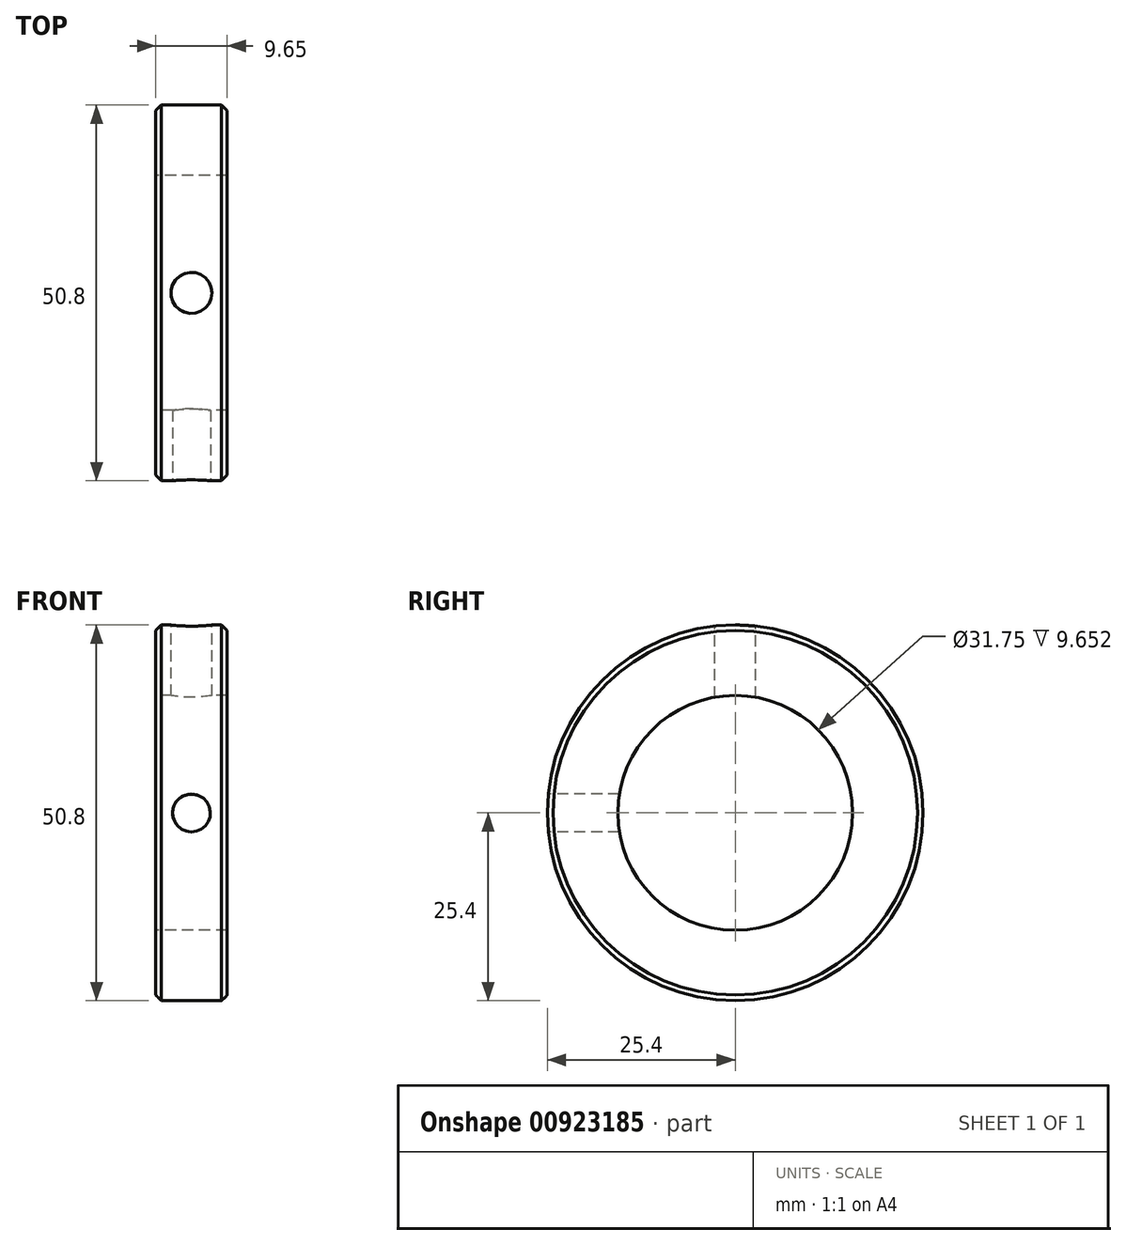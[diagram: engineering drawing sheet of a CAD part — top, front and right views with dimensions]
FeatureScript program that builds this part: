
annotation { "Feature Type Name" : "Feature", "Feature Type Description" : "" }
export const myFeature = defineFeature(function(context is Context, id is Id, definition is map)
    precondition{}
    {
        {
            var Q0;
            Q0=qCreatedBy(makeId("Right.planeOp"),FACE);
            var sketch = newSketch(context, id + "F0", { "sketchPlane" : qUnion([Q0])});
            skCircle(sketch, "E0", {"center": v(0, 0) * mm, "radius": 25.4 * mm});
            skCircle(sketch, "E1", {"center": v(0, 0) * mm, "radius": 15.88 * mm});
            skSolve(sketch);
        }
        {
            var Q0;
            Q0 = qSketchRegion(id + "F0", true);
            extrude(context, id + "F1", {"entities" : qUnion([Q0]), "depth" : 9.65 * mm, "offsetDistance" : 25.4 * mm});
        }
        {
            var Q0;
            Q0=makeQuery(id+"F1.opExtrude","CAP_EDGE",EDGE,{"disambiguationData":[OSD([sQuery(id+"F0.wireOp",EDGE,"E0")])],"isStart":false});
            chamfer(context, id + "F2", {"entities" : qUnion([Q0]), "width" : 0.76 * mm, "tangentPropagation" : true});
        }
        {
            var Q0;
            Q0=qCreatedBy(makeId("Front.planeOp"),FACE);
            cPlane(context, id + "F3", {"entities" : qUnion([Q0]), "cplaneType" : CPlaneType.OFFSET, "offset" : 25.4 * mm, "width" : 152.4 * mm, "height" : 152.4 * mm});
        }
        {
            var Q0;
            Q0=qCreatedBy(id+"F3.planeOp",FACE);
            var sketch = newSketch(context, id + "F4", { "sketchPlane" : qUnion([Q0])});
            skCircle(sketch, "E2", {"center": v(4.83, 0) * mm, "radius": 3.18 * mm});
            skSolve(sketch);
        }
        {
            var Q0;
            Q0=qCreatedBy(makeId("Top.planeOp"),FACE);
            cPlane(context, id + "F5", {"entities" : qUnion([Q0]), "cplaneType" : CPlaneType.OFFSET, "offset" : 25.4 * mm, "width" : 152.4 * mm, "height" : 152.4 * mm});
        }
        {
            var Q0;
            Q0=qCreatedBy(id+"F5.planeOp",FACE);
            var sketch = newSketch(context, id + "F6", { "sketchPlane" : qUnion([Q0])});
            skCircle(sketch, "E3", {"center": v(4.83, 0) * mm, "radius": 3.18 * mm});
            skSolve(sketch);
        }
        {
            var Q0;
            Q0=makeQuery(id+"F1.opExtrude","CAP_EDGE",EDGE,{"disambiguationData":[OSD([sQuery(id+"F0.wireOp",EDGE,"E0")])],"isStart":true});
            chamfer(context, id + "F7", {"entities" : qUnion([Q0]), "width" : 0.76 * mm, "tangentPropagation" : true});
        }
        {
            var Q0;
            Q0=sQuery(id+"F6.wireOp",VERTEX,"E3.center");
            var Q1;
            Q1=makeQuery(id+"F1.opExtrude","SWEPT_BODY",BODY,{"disambiguationData":[OSD([sQuery(id+"F0.wireOp",EDGE,"E0"),sQuery(id+"F0.wireOp",EDGE,"E1")])]});
            hole(context, id + "F8", {"style" : HoleStyle.SIMPLE, "endStyle" : HoleEndStyle.BLIND, "standardTappedOrClearance" : lookupTablePath({ "standard" : "ANSI", "engagement" : "50%", "pitch" : "20 tpi", "size" : "1/4", "type" : "Tapped" }), "standardBlindInLast" : lookupTablePath({ "standard" : "ANSI", "fit" : "Free", "engagement" : "50%", "pitch" : "20 tpi", "size" : "1/4", "type" : "Clearance & tapped" }), "holeDiameter" : 5.56 * mm, "majorDiameter" : 6.35 * mm, "showTappedDepth" : true, "holeDepth" : 16.51 * mm, "tappedDepth" : 10.16 * mm, "tapClearance" : 5, "startFromSketch" : true, "locations" : qUnion([Q0]), "scope" : qUnion([Q1])});
        }
        {
            var Q0;
            Q0=sQuery(id+"F4.wireOp",VERTEX,"E2.center");
            var Q1;
            Q1=makeQuery(id+"F1.opExtrude","SWEPT_BODY",BODY,{"disambiguationData":[OSD([sQuery(id+"F0.wireOp",EDGE,"E0"),sQuery(id+"F0.wireOp",EDGE,"E1")])]});
            hole(context, id + "F9", {"style" : HoleStyle.SIMPLE, "endStyle" : HoleEndStyle.BLIND, "standardTappedOrClearance" : lookupTablePath({ "standard" : "ANSI", "engagement" : "75%", "pitch" : "20 tpi", "size" : "1/4", "type" : "Tapped" }), "standardBlindInLast" : lookupTablePath({ "standard" : "ANSI", "fit" : "Free", "engagement" : "75%", "pitch" : "20 tpi", "size" : "1/4", "type" : "Clearance & tapped" }), "holeDiameter" : 5.1 * mm, "majorDiameter" : 6.35 * mm, "showTappedDepth" : true, "holeDepth" : 16.51 * mm, "tappedDepth" : 10.16 * mm, "tapClearance" : 5, "startFromSketch" : true, "locations" : qUnion([Q0]), "scope" : qUnion([Q1])});
        }
    });
